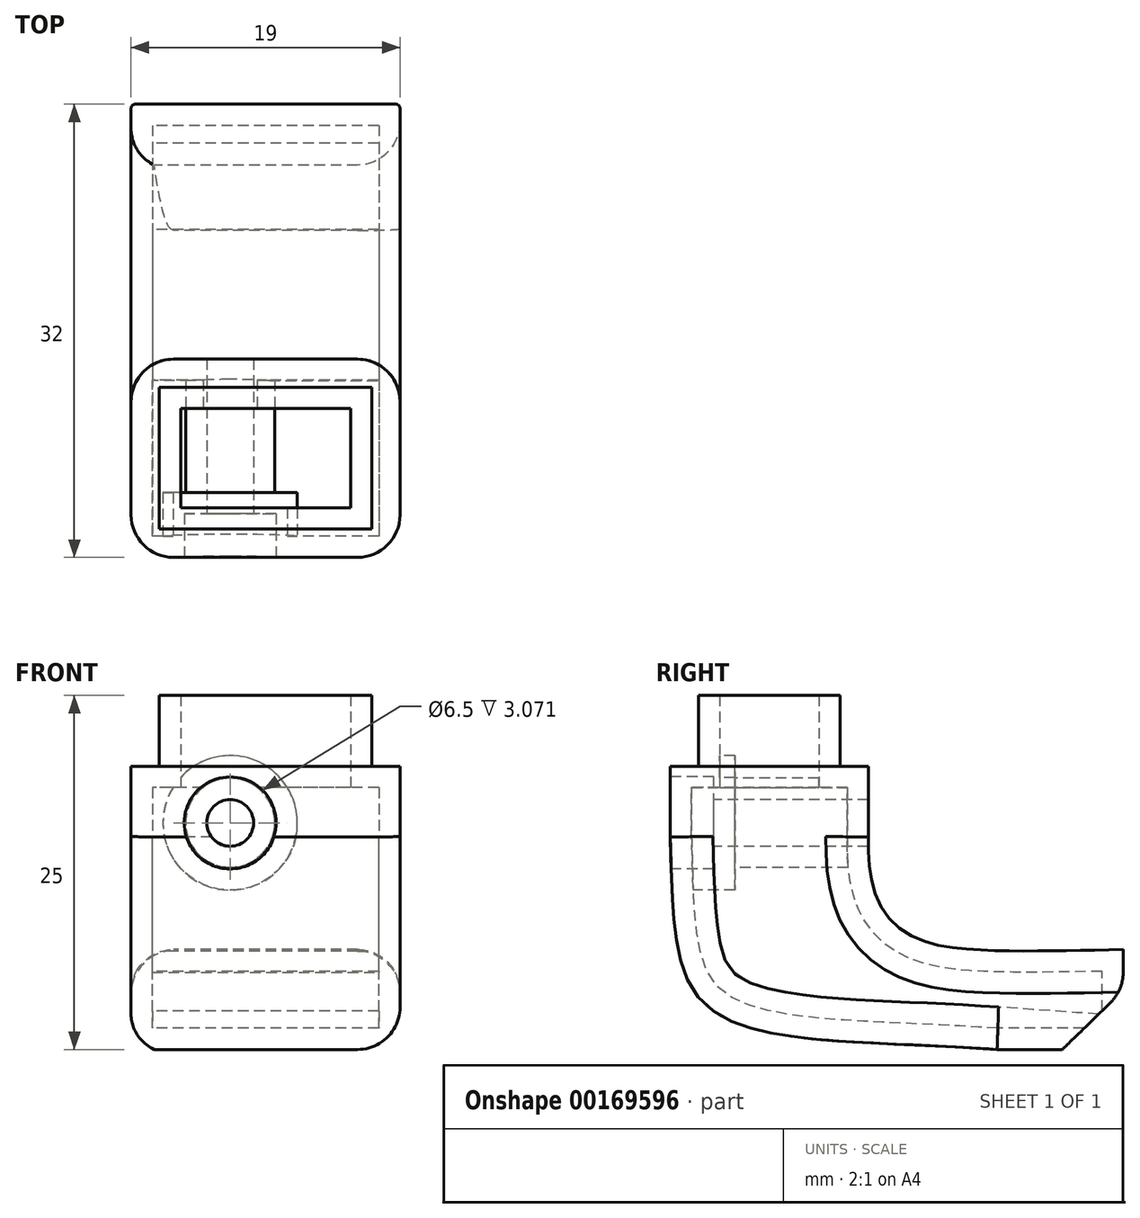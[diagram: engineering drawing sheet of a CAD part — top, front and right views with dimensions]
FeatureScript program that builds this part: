
annotation { "Feature Type Name" : "Feature", "Feature Type Description" : "" }
export const myFeature = defineFeature(function(context is Context, id is Id, definition is map)
    precondition{}
    {
        {
            var Q0;
            Q0=qCreatedBy(makeId("Right.planeOp"),FACE);
            var sketch = newSketch(context, id + "F0", { "sketchPlane" : qUnion([Q0])});
            skLineSegment(sketch, "E0.bottom", {"start": v(-12.05, 10) * mm, "end": v(-2.05, 10) * mm});
            skLineSegment(sketch, "E0.left", {"start": v(-12.05, 10) * mm, "end": v(-12.05, 5) * mm});
            skLineSegment(sketch, "E0.right", {"start": v(-2.05, 10) * mm, "end": v(-2.05, 5) * mm});
            skLineSegment(sketch, "E1", {"start": v(17.95, -10.82) * mm, "end": v(13.65, -15) * mm});
            skLineSegment(sketch, "E2", {"start": v(13.65, -15) * mm, "end": v(9.04, -15) * mm});
            skLineSegment(sketch, "E3", {"start": v(-12.05, 5) * mm, "end": v(-14.05, 5) * mm});
            skLineSegment(sketch, "E4", {"start": v(-14.05, 5) * mm, "end": v(-14.05, 0) * mm});
            skLineSegment(sketch, "E5", {"start": v(-2.05, 5) * mm, "end": v(-0.05, 5) * mm});
            skLineSegment(sketch, "E6", {"start": v(-0.05, 5) * mm, "end": v(-0.05, 0) * mm});
            skFitSpline(sketch, "E7", {"points": [v(9.04, -15) * mm, v(-11.26, -12.11) * mm, v(-14.05, 0) * mm], "startDerivative": vector(-48.24, 3.45) * mm, "endDerivative": vector(-1.37, 41.49) * mm});
            skLineSegment(sketch, "E8", {"start": v(17.95, -10.82) * mm, "end": v(17.95, -7.94) * mm});
            skFitSpline(sketch, "E9", {"points": [v(17.95, -7.94) * mm, v(2.41, -6.64) * mm, v(-0.05, 0) * mm], "startDerivative": vector(-50.55, -1.12) * mm, "endDerivative": vector(0.73, 29.27) * mm});
            skSolve(sketch);
        }
        {
            var Q0;
            Q0=makeQuery(id+"F0.imprint","IMPRINT",FACE,{"disambiguationData":[TD([[makeQuery(id+"F0.imprint","IMPRINT",EDGE,{"derivedFrom":sQuery(id+"F0.wireOp",EDGE,"E0.bottom")}),-1.0]])]});
            extrude(context, id + "F1", {"entities" : qUnion([Q0]), "endBound" : BoundingType.SYMMETRIC, "depth" : 19 * mm});
        }
        {
            var Q0;
            Q0=makeQuery(id+"F1.opExtrude","CAP_FACE",FACE,{"disambiguationData":[OSD([sQuery(id+"F0.wireOp",EDGE,"E0.bottom"),sQuery(id+"F0.wireOp",EDGE,"E0.left"),sQuery(id+"F0.wireOp",EDGE,"E0.right"),sQuery(id+"F0.wireOp",EDGE,"E1"),sQuery(id+"F0.wireOp",EDGE,"E2"),sQuery(id+"F0.wireOp",EDGE,"E3"),sQuery(id+"F0.wireOp",EDGE,"E4"),sQuery(id+"F0.wireOp",EDGE,"E5"),sQuery(id+"F0.wireOp",EDGE,"E6"),sQuery(id+"F0.wireOp",EDGE,"E7"),sQuery(id+"F0.wireOp",EDGE,"E8"),sQuery(id+"F0.wireOp",EDGE,"E9")])],"isStart":false});
            var sketch = newSketch(context, id + "F2", { "sketchPlane" : qUnion([Q0])});
            skLineSegment(sketch, "E10.bottom", {"start": v(-12.05, 10) * mm, "end": v(-2.05, 10) * mm});
            skLineSegment(sketch, "E10.top", {"start": v(-12.05, 5) * mm, "end": v(-2.05, 5) * mm});
            skLineSegment(sketch, "E10.left", {"start": v(-12.05, 10) * mm, "end": v(-12.05, 5) * mm});
            skLineSegment(sketch, "E10.right", {"start": v(-2.05, 10) * mm, "end": v(-2.05, 5) * mm});
            skSolve(sketch);
        }
        {
            var Q0;
            Q0=makeQuery(id+"F2.imprint","IMPRINT",FACE,{"disambiguationData":[TD([[makeQuery(id+"F2.imprint","IMPRINT",EDGE,{"derivedFrom":sQuery(id+"F2.wireOp",EDGE,"E10.bottom")}),-1.0]])]});
            extrude(context, id + "F3", {"entities" : qUnion([Q0]), "operationType" : NewBodyOperationType.REMOVE, "oppositeDirection" : true, "depth" : 2 * mm});
        }
        {
            var Q0;
            Q0=makeQuery(id+"F1.opExtrude","CAP_FACE",FACE,{"disambiguationData":[OSD([sQuery(id+"F0.wireOp",EDGE,"E0.bottom"),sQuery(id+"F0.wireOp",EDGE,"E0.left"),sQuery(id+"F0.wireOp",EDGE,"E0.right"),sQuery(id+"F0.wireOp",EDGE,"E1"),sQuery(id+"F0.wireOp",EDGE,"E2"),sQuery(id+"F0.wireOp",EDGE,"E3"),sQuery(id+"F0.wireOp",EDGE,"E4"),sQuery(id+"F0.wireOp",EDGE,"E5"),sQuery(id+"F0.wireOp",EDGE,"E6"),sQuery(id+"F0.wireOp",EDGE,"E7"),sQuery(id+"F0.wireOp",EDGE,"E8"),sQuery(id+"F0.wireOp",EDGE,"E9")])],"isStart":true});
            var sketch = newSketch(context, id + "F4", { "sketchPlane" : qUnion([Q0])});
            skLineSegment(sketch, "E11.bottom", {"start": v(2.05, 10) * mm, "end": v(12.05, 10) * mm});
            skLineSegment(sketch, "E11.top", {"start": v(2.05, 5) * mm, "end": v(12.05, 5) * mm});
            skLineSegment(sketch, "E11.left", {"start": v(2.05, 10) * mm, "end": v(2.05, 5) * mm});
            skLineSegment(sketch, "E11.right", {"start": v(12.05, 10) * mm, "end": v(12.05, 5) * mm});
            skSolve(sketch);
        }
        {
            var Q0;
            Q0=makeQuery(id+"F4.imprint","IMPRINT",FACE,{"disambiguationData":[TD([[makeQuery(id+"F4.imprint","IMPRINT",EDGE,{"derivedFrom":sQuery(id+"F4.wireOp",EDGE,"E11.bottom")}),1.0]])]});
            extrude(context, id + "F5", {"entities" : qUnion([Q0]), "operationType" : NewBodyOperationType.REMOVE, "oppositeDirection" : true, "depth" : 2 * mm});
        }
        {
            var Q0;
            Q0=makeQuery(id+"F1.opExtrude","SWEPT_FACE",FACE,{"disambiguationData":[OSD([sQuery(id+"F0.wireOp",EDGE,"E4")])]});
            var sketch = newSketch(context, id + "F6", { "sketchPlane" : qUnion([Q0])});
            skPoint(sketch, "E12", {"position": v(-2.5, 1) * mm});
            skSolve(sketch);
        }
        {
            var Q0;
            Q0=sQuery(id+"F6.wireOp",VERTEX,"E12");
            var Q1;
            Q1=makeQuery(id+"F1.opExtrude","SWEPT_BODY",BODY,{"disambiguationData":[OSD([sQuery(id+"F0.wireOp",EDGE,"E0.bottom"),sQuery(id+"F0.wireOp",EDGE,"E0.left"),sQuery(id+"F0.wireOp",EDGE,"E0.right"),sQuery(id+"F0.wireOp",EDGE,"E1"),sQuery(id+"F0.wireOp",EDGE,"E2"),sQuery(id+"F0.wireOp",EDGE,"E3"),sQuery(id+"F0.wireOp",EDGE,"E4"),sQuery(id+"F0.wireOp",EDGE,"E5"),sQuery(id+"F0.wireOp",EDGE,"E6"),sQuery(id+"F0.wireOp",EDGE,"E7"),sQuery(id+"F0.wireOp",EDGE,"E8"),sQuery(id+"F0.wireOp",EDGE,"E9")])]});
            hole(context, id + "F7", {"style" : HoleStyle.C_BORE, "endStyle" : HoleEndStyle.THROUGH, "standardTappedOrClearance" : lookupTablePath({ "standard" : "ISO", "fit" : "Normal", "size" : "M3", "type" : "Clearance" }), "standardBlindInLast" : lookupTablePath({ "fit" : "Standard", "standard" : "ISO", "size" : "M3", "type" : "Clearance" }), "holeDiameter" : 3.3 * mm, "cBoreDiameter" : 6.5 * mm, "cBoreDepth" : 3 * mm, "locations" : qUnion([Q0]), "scope" : qUnion([Q1]), "isTappedThrough" : true});
        }
        {
            var Q0;
            Q0=makeQuery(id+"F1.opExtrude","SWEPT_FACE",FACE,{"disambiguationData":[OSD([sQuery(id+"F0.wireOp",EDGE,"E0.bottom")])]});
            var Q1;
            Q1=makeQuery(id+"F1.opExtrude","SWEPT_FACE",FACE,{"disambiguationData":[OSD([sQuery(id+"F0.wireOp",EDGE,"E1")])]});
            shell(context, id + "F8", {"entities" : qUnion([Q0, Q1]), "thickness" : 1.5 * mm});
        }
        {
            var Q0;
            Q0=makeQuery(id+"F1.opExtrude","CAP_EDGE",EDGE,{"disambiguationData":[OSD([sQuery(id+"F0.wireOp",EDGE,"E6")])],"isStart":false});
            var Q1;
            Q1=makeQuery(id+"F1.opExtrude","CAP_EDGE",EDGE,{"disambiguationData":[OSD([sQuery(id+"F0.wireOp",EDGE,"E9")])],"isStart":false});
            var Q2;
            Q2=makeQuery(id+"F1.opExtrude","CAP_EDGE",EDGE,{"disambiguationData":[OSD([sQuery(id+"F0.wireOp",EDGE,"E7")])],"isStart":false});
            var Q3;
            Q3=makeQuery(id+"F1.opExtrude","CAP_EDGE",EDGE,{"disambiguationData":[OSD([sQuery(id+"F0.wireOp",EDGE,"E4")])],"isStart":false});
            var Q4;
            Q4=makeQuery(id+"F1.opExtrude","CAP_EDGE",EDGE,{"disambiguationData":[OSD([sQuery(id+"F0.wireOp",EDGE,"E2")])],"isStart":false});
            var Q5;
            Q5=makeQuery(id+"F1.opExtrude","CAP_EDGE",EDGE,{"disambiguationData":[OSD([sQuery(id+"F0.wireOp",EDGE,"E9")])],"isStart":true});
            var Q6;
            Q6=makeQuery(id+"F1.opExtrude","CAP_EDGE",EDGE,{"disambiguationData":[OSD([sQuery(id+"F0.wireOp",EDGE,"E6")])],"isStart":true});
            var Q7;
            Q7=makeQuery(id+"F1.opExtrude","CAP_EDGE",EDGE,{"disambiguationData":[OSD([sQuery(id+"F0.wireOp",EDGE,"E4")])],"isStart":true});
            var Q8;
            Q8=makeQuery(id+"F1.opExtrude","CAP_EDGE",EDGE,{"disambiguationData":[OSD([sQuery(id+"F0.wireOp",EDGE,"E7")])],"isStart":true});
            var Q9;
            Q9=makeQuery(id+"F1.opExtrude","SWEPT_EDGE",EDGE,{"disambiguationData":[OSD([sQuery(id+"F0.wireOp",EDGE,"E1"),sQuery(id+"F0.wireOp",EDGE,"E8")])]});
            fillet(context, id + "F9", {"entities" : qUnion([Q0, Q1, Q2, Q3, Q4, Q5, Q6, Q7, Q8, Q9]), "radius" : 3 * mm, "tangentPropagation" : true, "allowEdgeOverflow" : false});
        }
    });
